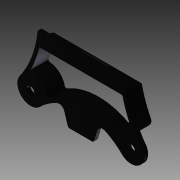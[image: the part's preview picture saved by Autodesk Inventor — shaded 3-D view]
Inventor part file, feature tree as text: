
AUTODESK INVENTOR PART (.ipt)
format: ipt  version: 2015 (Build 190159000, 159)  size: 631,808 bytes
history: native  units: mm
features: extrude x16, sketch x16, fillet x10, projected_geometry x7, plane x2
ambient origin geometry x8: Origin, YZ Plane, XZ Plane, XY Plane, X Axis, Y Axis, Z Axis, Center Point
bodies: Solid1 (feature_tree)
feature tree (51):
  extrude  "Extrusion1"  Depth=3.5mm
  extrude  "Extrusion2"  Depth=3.5mm TaperAngle=0.0deg
  extrude  "Extrusion3"  Depth=3.5mm TaperAngle=0.0deg
  extrude  "Extrusion4"  Depth=13.5mm TaperAngle=0.0deg
  extrude  "Extrusion5"  Depth=13.5mm TaperAngle=0.0deg
  extrude  "Extrusion6"  Depth=13.5mm TaperAngle=0.0deg
  extrude  "Extrusion8"  Depth=3.5mm TaperAngle=0.0deg
  extrude  "Extrusion9"  Depth=4.4125mm
  extrude  "Extrusion10"  TaperAngle=45.0deg  [1 undecoded]
  plane  "Work Plane1"
  extrude  "Extrusion11"  Depth=3.5mm
  fillet  "Fillet4"  Radius=3.5mm
  fillet  "Fillet5"  Radius=1.0mm
  fillet  "Fillet6"  Radius=1.0mm
  fillet  "Fillet7"  Radius=1.0mm
  fillet  "Fillet8"  Radius=3.5mm
  fillet  "Fillet9"  Radius=1.0mm
  fillet  "Fillet10"  Radius=10.0mm
  extrude  "Extrusion14"  Depth=12.5mm
  extrude  "Extrusion15"  Depth=5.0mm
  fillet  "Fillet11"  [1 undecoded]
  fillet  "Fillet12"  Radius=25.0mm
  extrude  "Extrusion16"  Depth=2.5mm
  plane  "Work Plane3"
  extrude  "Extrusion17"  Depth=1.0mm
  extrude  "Extrusion18"  Depth=7.0mm
  extrude  "Extrusion19"  Depth=0.95mm TaperAngle=0.0deg
  fillet  "Fillet13"  [1 undecoded]
  sketch  "Sketch1"  dims[d13=3.5mm d16=3.5mm]
  sketch  "Sketch2"  dims[d24=90.0deg d25=3.5mm d26=0.0mm]
  sketch  "Sketch3"  dims[d30=8.907301mm d32=3.5mm d33=0.0mm]
  projected_geometry  "Projected Loop1"
  sketch  "Sketch4"  dims[d34=13.5mm d35=0.0mm d38=13.5mm d39=0.0mm]
  sketch  "Sketch5"  dims[d40=31.55mm d41=13.5mm d42=0.0mm]
  projected_geometry  "Projected Loop2"
  sketch  "Sketch7"  dims[d44=3.5mm d45=0.0mm d51=13.5mm d52=0.0mm]
  projected_geometry  "Projected Loop3"
  sketch  "Sketch13"  dims[d53=3.5mm d54=0.0mm d55=3.5mm d56=0.0mm]
  projected_geometry  "Projected Loop5"
  sketch  "Sketch14"  dims[d57=0.0mm d58=4.4125mm]
  projected_geometry  "Projected Loop6"
  sketch  "Sketch15"  dims[d59=90.0deg d60=45.0deg]
  projected_geometry  "Projected Loop7"
  sketch  "Sketch16"  dims[d61=50.0mm d62=0.0mm d67=3.5mm d68=3.5mm d69=1.0mm d70=1.0mm d75=1.0mm d103=3.5mm d104=1.0mm d108=10.0mm d109=0.0mm]
  sketch  "Sketch27"  dims[d110=180.0deg d111=12.5mm]
  sketch  "Sketch28"  dims[d113=25.0mm d115=5.0mm d116=90.0deg d117=25.0mm]
  projected_geometry  "Projected Loop11"
  sketch  "Sketch29"  dims[d118=90.0deg d119=2.5mm]
  sketch  "Sketch32"  dims[d120=30.0mm d121=0.0mm d122=1.0mm]
  sketch  "Sketch33"  dims[d123=1.0mm d124=7.0mm]
  sketch  "Sketch34"  dims[d125=7.0mm d126=3.5mm d127=0.0mm d151=0.0mm d172=3.5mm d173=0.0mm d174=3.5mm d175=0.0mm d176=46.987913mm d177=12.022738mm d178=3.5mm d179=3.5mm d180=0.0mm d181=0.95mm]
note: 3 required parameter values undecoded (feature->parameter linkage not recoverable at this tier; creation-order binding heuristic only, values carry confidence <= 0.55)
